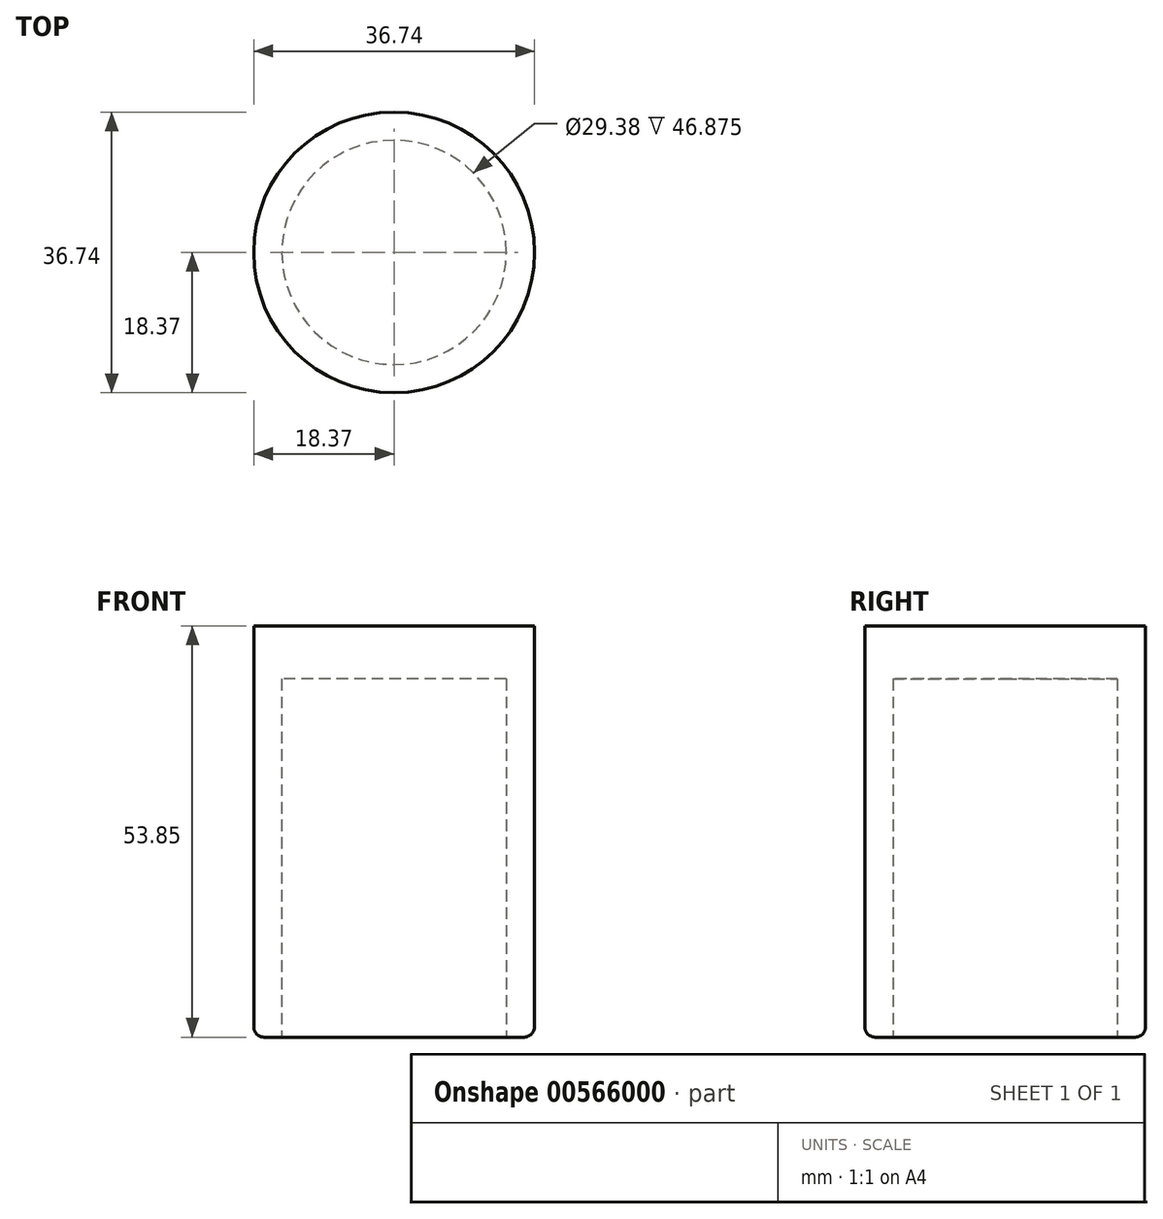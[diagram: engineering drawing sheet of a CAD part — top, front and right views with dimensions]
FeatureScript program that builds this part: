
annotation { "Feature Type Name" : "Feature", "Feature Type Description" : "" }
export const myFeature = defineFeature(function(context is Context, id is Id, definition is map)
    precondition{}
    {
        {
            var Q0;
            Q0=qCreatedBy(makeId("Top.planeOp"),FACE);
            var sketch = newSketch(context, id + "F0", { "sketchPlane" : qUnion([Q0])});
            skCircle(sketch, "E0", {"center": v(0, 0) * mm, "radius": 18.37 * mm});
            skCircle(sketch, "E1", {"center": v(0, 0) * mm, "radius": 14.69 * mm});
            skSolve(sketch);
        }
        {
            var Q0;
            Q0=makeQuery(id+"F0.imprint","IMPRINT",FACE,{"disambiguationData":[TD([[makeQuery(id+"F0.imprint","IMPRINT",EDGE,{"derivedFrom":sQuery(id+"F0.wireOp",EDGE,"E1")}),1.0]])]});
            var Q1;
            Q1=makeQuery(id+"F0.imprint","IMPRINT",FACE,{"disambiguationData":[TD([[makeQuery(id+"F0.imprint","IMPRINT",EDGE,{"derivedFrom":sQuery(id+"F0.wireOp",EDGE,"E0")}),1.0]])]});
            extrude(context, id + "F1", {"entities" : qUnion([Q0, Q1]), "depth" : 53.85 * mm, "offsetDistance" : 25 * mm});
        }
        {
            var Q0;
            Q0=makeQuery(id+"F0.imprint","IMPRINT",FACE,{"disambiguationData":[TD([[makeQuery(id+"F0.imprint","IMPRINT",EDGE,{"derivedFrom":sQuery(id+"F0.wireOp",EDGE,"E1")}),1.0]])]});
            extrude(context, id + "F2", {"entities" : qUnion([Q0]), "operationType" : NewBodyOperationType.REMOVE, "depth" : 46.88 * mm, "offsetDistance" : 25 * mm});
        }
        {
            var Q0;
            Q0=makeQuery(id+"F2.boolean.opBoolean","COPY",EDGE,{"derivedFrom":makeQuery(id+"F2.opExtrude","CAP_EDGE",EDGE,{"disambiguationData":[OSD([sQuery(id+"F0.wireOp",EDGE,"E1")])],"isStart":true})});
            var Q1;
            Q1=makeQuery(id+"F1.opExtrude","CAP_EDGE",EDGE,{"disambiguationData":[OSD([sQuery(id+"F0.wireOp",EDGE,"E0")])],"isStart":true});
            fillet(context, id + "F3", {"entities" : qUnion([Q0, Q1]), "radius" : 1.37 * mm, "tangentPropagation" : true, "allowEdgeOverflow" : false});
        }
    });
